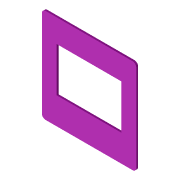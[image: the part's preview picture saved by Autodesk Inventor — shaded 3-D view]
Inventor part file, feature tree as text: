
AUTODESK INVENTOR PART (.ipt)
format: ipt  version: 2022 (Build 260153000, 153)  size: 91,648 bytes
history: native  units: mm
features: extrude x1, sketch x1
ambient origin geometry x8: Origin, YZ Plane, XZ Plane, XY Plane, X Axis, Y Axis, Z Axis, Center Point
bodies: Volumenkörper1 (feature_tree)
feature tree (2):
  extrude  "Extrusion1"  Depth=51.0mm
  sketch  "Skizze1"  dims[d0=51.0mm d1=51.0mm d2=35.0mm d3=24.0mm d4=12.5mm d5=2.0mm d6=1.0mm d7=0.0mm]
